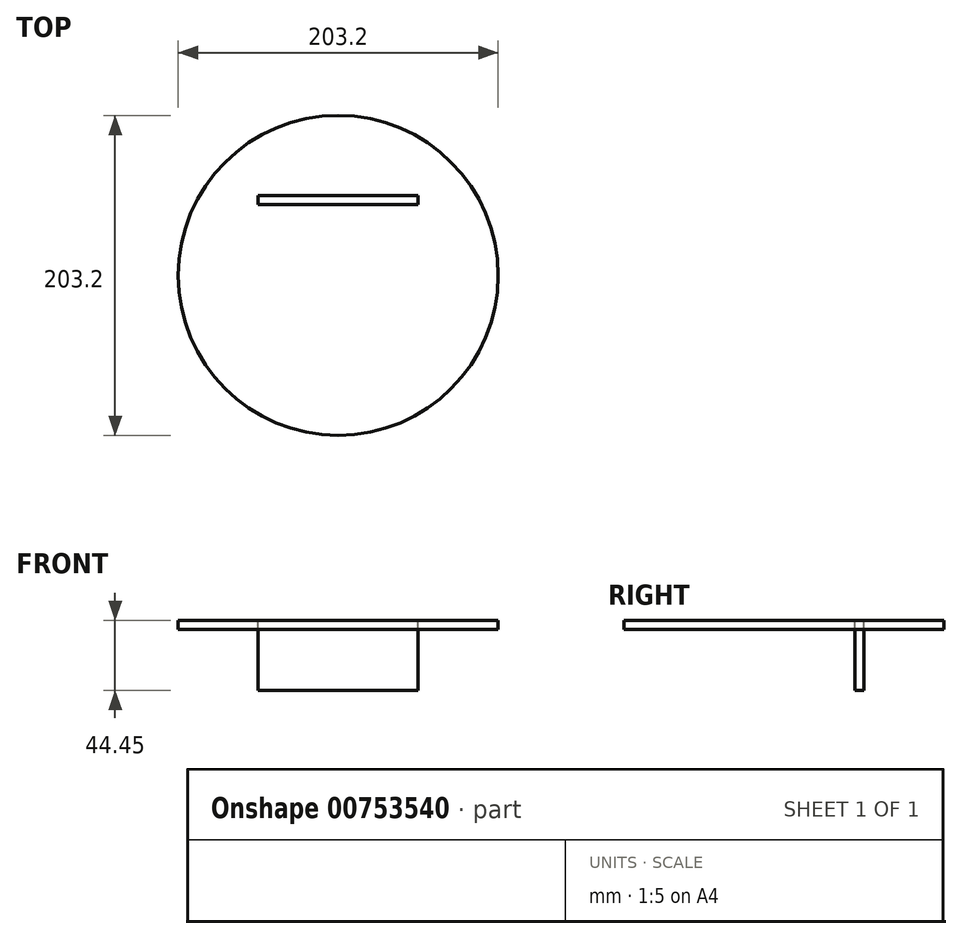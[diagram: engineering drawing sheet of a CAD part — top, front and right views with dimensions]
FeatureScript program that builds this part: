
annotation { "Feature Type Name" : "Feature", "Feature Type Description" : "" }
export const myFeature = defineFeature(function(context is Context, id is Id, definition is map)
    precondition{}
    {
        {
            var Q0;
            Q0=qCreatedBy(makeId("Top.planeOp"),FACE);
            var sketch = newSketch(context, id + "F0", { "sketchPlane" : qUnion([Q0])});
            skCircle(sketch, "E0", {"center": v(0, 0) * mm, "radius": 101.6 * mm});
            skSolve(sketch);
        }
        {
            var Q0;
            Q0=makeQuery(id+"F0.imprint","IMPRINT",FACE,{"disambiguationData":[TD([[makeQuery(id+"F0.imprint","IMPRINT",EDGE,{"derivedFrom":sQuery(id+"F0.wireOp",EDGE,"E0")}),1.0]])]});
            extrude(context, id + "F1", {"entities" : qUnion([Q0]), "depth" : 5.7 * mm, "offsetDistance" : 25.4 * mm});
        }
        {
            var Q0;
            Q0=makeQuery(id+"F1.opExtrude","CAP_FACE",FACE,{"disambiguationData":[OSD([sQuery(id+"F0.wireOp",EDGE,"E0")])],"isStart":false});
            var sketch = newSketch(context, id + "F2", { "sketchPlane" : qUnion([Q0])});
            skLineSegment(sketch, "E1.bottom", {"start": v(-50.8, 50.8) * mm, "end": v(50.8, 50.8) * mm, "construction": true});
            skLineSegment(sketch, "E1.top", {"start": v(-50.8, -50.8) * mm, "end": v(50.8, -50.8) * mm, "construction": true});
            skLineSegment(sketch, "E1.left", {"start": v(-50.8, 50.8) * mm, "end": v(-50.8, -50.8) * mm, "construction": true});
            skLineSegment(sketch, "E1.right", {"start": v(50.8, 50.8) * mm, "end": v(50.8, -50.8) * mm, "construction": true});
            skLineSegment(sketch, "E2", {"start": v(0, 0) * mm, "end": v(0, 50.8) * mm, "construction": true});
            skLineSegment(sketch, "E3", {"start": v(0, 0) * mm, "end": v(50.8, 0) * mm, "construction": true});
            skLineSegment(sketch, "E4.bottom", {"start": v(-50.8, 50.8) * mm, "end": v(50.8, 50.8) * mm});
            skLineSegment(sketch, "E4.top", {"start": v(-50.8, 45.11) * mm, "end": v(50.8, 45.11) * mm});
            skLineSegment(sketch, "E4.left", {"start": v(-50.8, 50.8) * mm, "end": v(-50.8, 45.11) * mm});
            skLineSegment(sketch, "E4.right", {"start": v(50.8, 50.8) * mm, "end": v(50.8, 45.11) * mm});
            skSolve(sketch);
        }
        {
            var Q0;
            Q0=makeQuery(id+"F2.imprint","IMPRINT",FACE,{"disambiguationData":[TD([[makeQuery(id+"F2.imprint","IMPRINT",EDGE,{"derivedFrom":sQuery(id+"F2.wireOp",EDGE,"E4.bottom")}),-1.0]])]});
            extrude(context, id + "F3", {"entities" : qUnion([Q0]), "oppositeDirection" : true, "depth" : 44.45 * mm, "offsetDistance" : 25.4 * mm});
        }
    });
